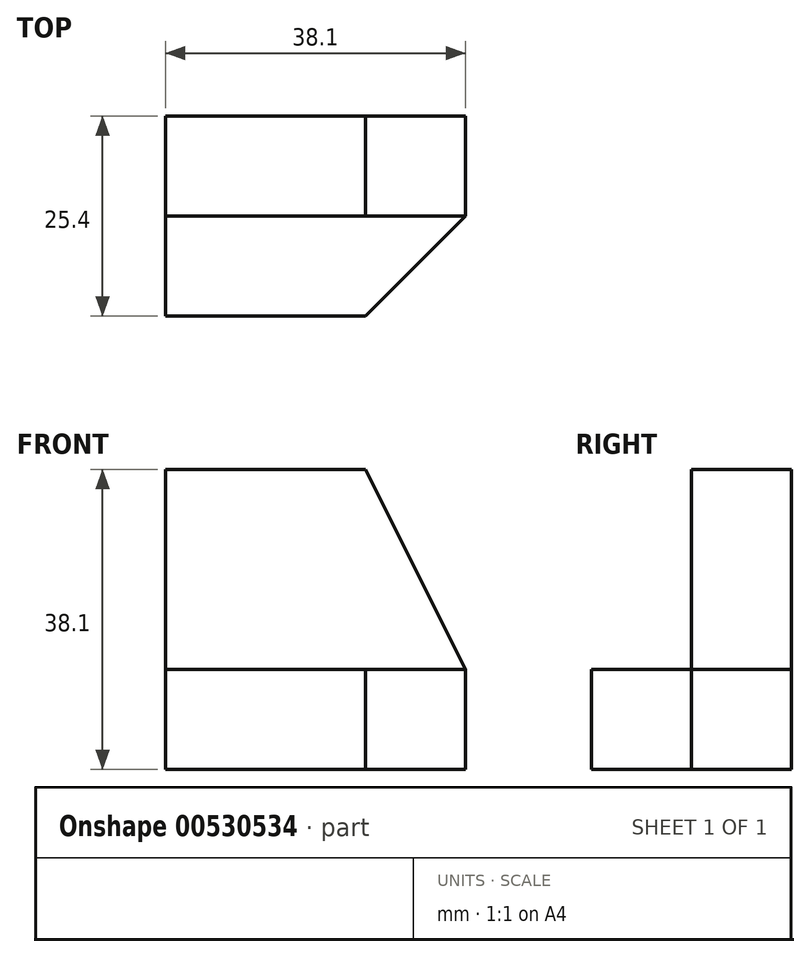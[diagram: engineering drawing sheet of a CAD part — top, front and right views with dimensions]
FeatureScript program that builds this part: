
annotation { "Feature Type Name" : "Feature", "Feature Type Description" : "" }
export const myFeature = defineFeature(function(context is Context, id is Id, definition is map)
    precondition{}
    {
        {
            var Q0;
            Q0=qCreatedBy(makeId("Front.planeOp"),FACE);
            var sketch = newSketch(context, id + "F0", { "sketchPlane" : qUnion([Q0])});
            skLineSegment(sketch, "E0", {"start": v(-65.04, 46.24) * mm, "end": v(-65.04, 8.14) * mm});
            skLineSegment(sketch, "E1", {"start": v(-65.04, 8.14) * mm, "end": v(-26.94, 8.14) * mm});
            skLineSegment(sketch, "E2", {"start": v(-26.94, 8.14) * mm, "end": v(-26.94, 20.84) * mm});
            skLineSegment(sketch, "E3", {"start": v(-65.04, 46.24) * mm, "end": v(-39.64, 46.24) * mm});
            skLineSegment(sketch, "E4", {"start": v(-39.64, 46.24) * mm, "end": v(-26.94, 20.84) * mm});
            skSolve(sketch);
        }
        {
            var Q0;
            Q0 = qSketchRegion(id + "F0", true);
            extrude(context, id + "F1", {"entities" : qUnion([Q0]), "depth" : 12.7 * mm, "offsetDistance" : 25.4 * mm});
        }
        {
            var Q0;
            Q0=makeQuery(id+"F1.opExtrude","CAP_FACE",FACE,{"disambiguationData":[OSD([sQuery(id+"F0.wireOp",EDGE,"E0"),sQuery(id+"F0.wireOp",EDGE,"E1"),sQuery(id+"F0.wireOp",EDGE,"E2"),sQuery(id+"F0.wireOp",EDGE,"E3"),sQuery(id+"F0.wireOp",EDGE,"E4")])],"isStart":false});
            var sketch = newSketch(context, id + "F2", { "sketchPlane" : qUnion([Q0])});
            skLineSegment(sketch, "E5", {"start": v(-65.04, 8.14) * mm, "end": v(-26.94, 8.14) * mm});
            skLineSegment(sketch, "E6", {"start": v(-26.94, 8.14) * mm, "end": v(-26.94, 20.84) * mm});
            skLineSegment(sketch, "E7", {"start": v(-26.94, 20.84) * mm, "end": v(-65.04, 20.84) * mm});
            skLineSegment(sketch, "E8", {"start": v(-65.04, 20.84) * mm, "end": v(-65.04, 8.14) * mm});
            skSolve(sketch);
        }
        {
            var Q0;
            Q0=makeQuery(id+"F2.imprint","IMPRINT",FACE,{"disambiguationData":[TD([[makeQuery(id+"F2.imprint","IMPRINT",EDGE,{"derivedFrom":sQuery(id+"F2.wireOp",EDGE,"E5")}),1.0]])]});
            extrude(context, id + "F3", {"entities" : qUnion([Q0]), "operationType" : NewBodyOperationType.ADD, "depth" : 12.7 * mm, "offsetDistance" : 25.4 * mm});
        }
        {
            var Q0;
            Q0=makeQuery(id+"F3.opExtrude","SWEPT_FACE",FACE,{"disambiguationData":[OSD([sQuery(id+"F2.wireOp",EDGE,"E7")])]});
            var sketch = newSketch(context, id + "F4", { "sketchPlane" : qUnion([Q0])});
            skLineSegment(sketch, "E9", {"start": v(-26.94, -12.7) * mm, "end": v(-39.64, -25.4) * mm});
            skSolve(sketch);
        }
        {
            var Q0;
            {var subQ0=sQuery(id+"F4.wireOp",EDGE,"E9");Q0=makeQuery(id+"F4.imprint","IMPRINT",FACE,{"disambiguationData":[TD([[makeQuery(id+"F4.imprint","IMPRINT",EDGE,{"derivedFrom":subQ0}),1.0]])]});}
            extrude(context, id + "F5", {"entities" : qUnion([Q0]), "operationType" : NewBodyOperationType.REMOVE, "endBound" : BoundingType.THROUGH_ALL, "oppositeDirection" : true, "depth" : 25.4 * mm, "offsetDistance" : 25.4 * mm});
        }
    });
